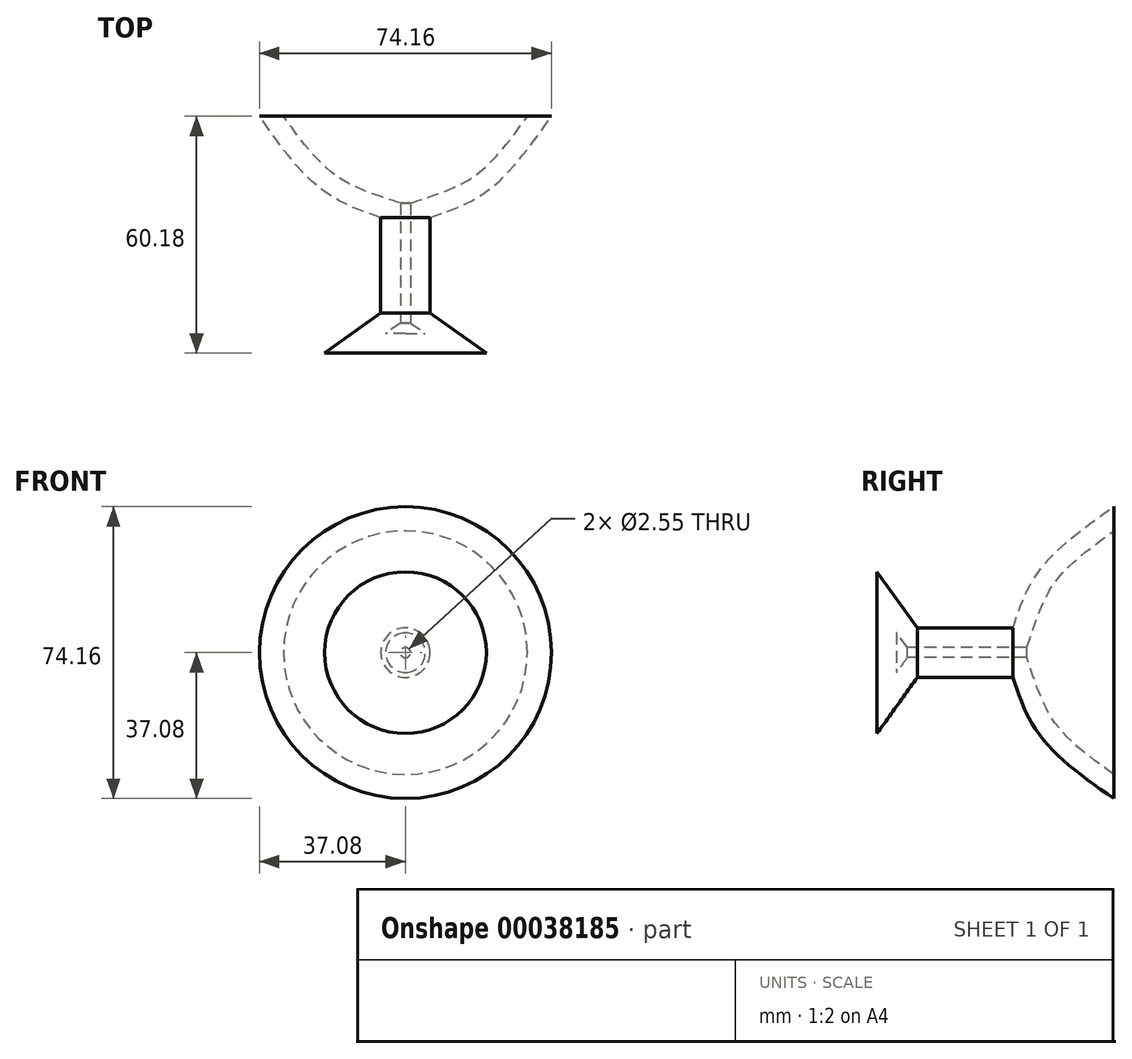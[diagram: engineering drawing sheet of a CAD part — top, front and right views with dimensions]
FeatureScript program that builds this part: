
annotation { "Feature Type Name" : "Feature", "Feature Type Description" : "" }
export const myFeature = defineFeature(function(context is Context, id is Id, definition is map)
    precondition{}
    {
        {
            var Q0;
            Q0=qCreatedBy(makeId("Top.planeOp"),FACE);
            var sketch = newSketch(context, id + "F0", { "sketchPlane" : qUnion([Q0])});
            skLineSegment(sketch, "E0", {"start": v(0, 22.96) * mm, "end": v(37.08, 22.96) * mm});
            skFitSpline(sketch, "E1", {"points": [v(37.08, 22.96) * mm, v(21.4, 4.42) * mm, v(6.28, -2.7) * mm], "startDerivative": vector(-27.44, -38.9) * mm, "endDerivative": vector(-34.4, -11.6) * mm});
            skLineSegment(sketch, "E2", {"start": v(6.28, -2.7) * mm, "end": v(6.28, -26.96) * mm});
            skLineSegment(sketch, "E3", {"start": v(6.28, -26.96) * mm, "end": v(20.54, -37.22) * mm});
            skLineSegment(sketch, "E4", {"start": v(20.54, -37.22) * mm, "end": v(0, -37.22) * mm});
            skLineSegment(sketch, "E5", {"start": v(0, -37.22) * mm, "end": v(0, 22.96) * mm});
            skSolve(sketch);
        }
        {
            var Q0;
            Q0=makeQuery(id+"F0.imprint","IMPRINT",FACE,{"disambiguationData":[TD([[makeQuery(id+"F0.imprint","IMPRINT",EDGE,{"derivedFrom":sQuery(id+"F0.wireOp",EDGE,"E0")}),-1.0]])]});
            var Q1;
            Q1=sQuery(id+"F0.wireOp",EDGE,"E5");
            revolve(context, id + "F1", {"entities" : qUnion([Q0]), "axis" : qUnion([Q1]), "revolveType" : RevolveType.FULL});
        }
        {
            var Q0;
            Q0=makeQuery(id+"F1.opRevolve","SWEPT_FACE",FACE,{"disambiguationData":[OSD([sQuery(id+"F0.wireOp",EDGE,"E0")])]});
            shell(context, id + "F2", {"entities" : qUnion([Q0]), "thickness" : 5 * mm});
        }
    });
